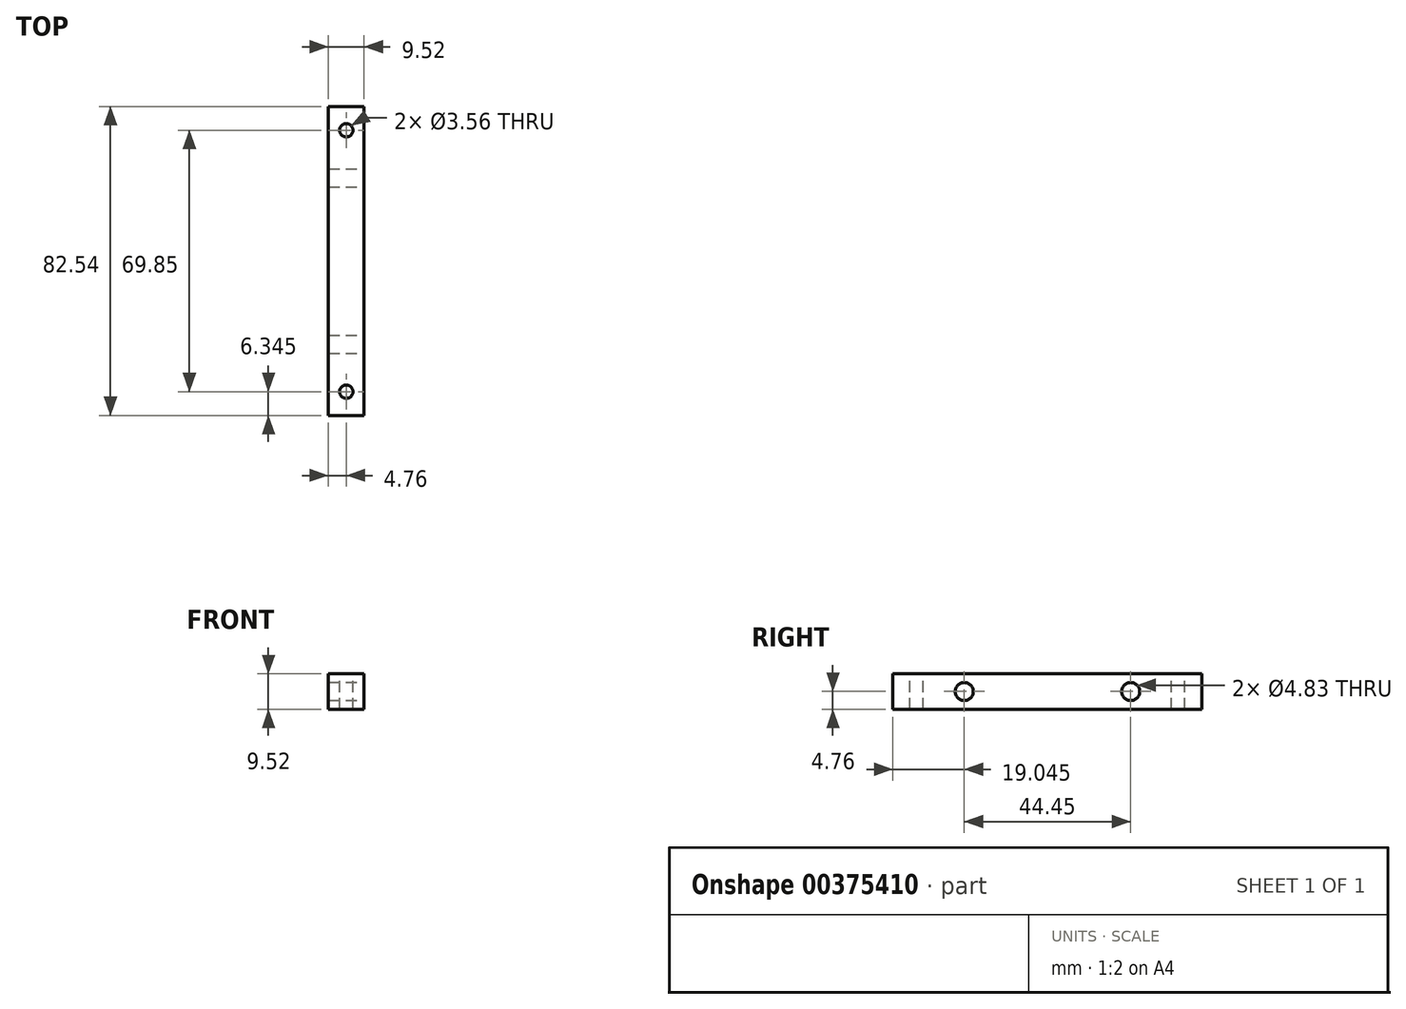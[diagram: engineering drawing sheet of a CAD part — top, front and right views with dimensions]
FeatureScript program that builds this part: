
annotation { "Feature Type Name" : "Feature", "Feature Type Description" : "" }
export const myFeature = defineFeature(function(context is Context, id is Id, definition is map)
    precondition{}
    {
        {
            var Q0;
            Q0=qCreatedBy(makeId("Front.planeOp"),FACE);
            var sketch = newSketch(context, id + "F0", { "sketchPlane" : qUnion([Q0])});
            skLineSegment(sketch, "E0.bottom", {"start": v(-4.76, 4.76) * mm, "end": v(4.76, 4.76) * mm});
            skLineSegment(sketch, "E0.top", {"start": v(-4.76, -4.76) * mm, "end": v(4.76, -4.76) * mm});
            skLineSegment(sketch, "E0.left", {"start": v(-4.76, 4.76) * mm, "end": v(-4.76, -4.76) * mm});
            skLineSegment(sketch, "E0.right", {"start": v(4.76, 4.76) * mm, "end": v(4.76, -4.76) * mm});
            skPoint(sketch, "E0.middle", {"position": v(0, 0) * mm});
            skSolve(sketch);
        }
        {
            var Q0;
            Q0=qSketchRegion(id+"F0",true);
            extrude(context, id + "F1", {"entities" : qUnion([Q0]), "depth" : 82.55 * mm, "symmetric" : true});
        }
        {
            var Q0;
            Q0=makeQuery(id+"F1.opExtrude","SWEPT_FACE",FACE,{"disambiguationData":[OSD([sQuery(id+"F0.wireOp",EDGE,"E0.bottom")])]});
            var sketch = newSketch(context, id + "F2", { "sketchPlane" : qUnion([Q0])});
            skLineSegment(sketch, "E1", {"start": v(0, 0) * mm, "end": v(0, -34.93) * mm, "construction": true});
            skCircle(sketch, "E2", {"center": v(0, -34.93) * mm, "radius": 1.78 * mm});
            skSolve(sketch);
        }
        {
            var Q0;
            Q0=qSketchRegion(id+"F2",true);
            extrude(context, id + "F3", {"entities" : qUnion([Q0]), "operationType" : NewBodyOperationType.REMOVE, "endBound" : BoundingType.THROUGH_ALL, "oppositeDirection" : true, "depth" : 25.4 * mm});
        }
        {
            var Q0;
            Q0=makeQuery(id+"F1.opExtrude","SWEPT_FACE",FACE,{"disambiguationData":[OSD([sQuery(id+"F0.wireOp",EDGE,"E0.bottom")])]});
            var sketch = newSketch(context, id + "F4", { "sketchPlane" : qUnion([Q0])});
            skLineSegment(sketch, "E3", {"start": v(0, 0) * mm, "end": v(0, 34.93) * mm, "construction": true});
            skCircle(sketch, "E4", {"center": v(0, 34.93) * mm, "radius": 1.78 * mm});
            skSolve(sketch);
        }
        {
            var Q0;
            Q0=qSketchRegion(id+"F4",true);
            extrude(context, id + "F5", {"entities" : qUnion([Q0]), "operationType" : NewBodyOperationType.REMOVE, "endBound" : BoundingType.THROUGH_ALL, "oppositeDirection" : true, "depth" : 25.4 * mm});
        }
        {
            var Q0;
            Q0=makeQuery(id+"F1.opExtrude","SWEPT_FACE",FACE,{"disambiguationData":[OSD([sQuery(id+"F0.wireOp",EDGE,"E0.right")])]});
            var sketch = newSketch(context, id + "F6", { "sketchPlane" : qUnion([Q0])});
            skLineSegment(sketch, "E5", {"start": v(0, 0) * mm, "end": v(-22.23, 0) * mm, "construction": true});
            skCircle(sketch, "E6", {"center": v(-22.23, 0) * mm, "radius": 2.41 * mm});
            skSolve(sketch);
        }
        {
            var Q0;
            Q0=qSketchRegion(id+"F6",true);
            extrude(context, id + "F7", {"entities" : qUnion([Q0]), "operationType" : NewBodyOperationType.REMOVE, "endBound" : BoundingType.THROUGH_ALL, "oppositeDirection" : true, "depth" : 25.4 * mm});
        }
        {
            var Q0;
            Q0=makeQuery(id+"F1.opExtrude","SWEPT_FACE",FACE,{"disambiguationData":[OSD([sQuery(id+"F0.wireOp",EDGE,"E0.right")])]});
            var sketch = newSketch(context, id + "F8", { "sketchPlane" : qUnion([Q0])});
            skLineSegment(sketch, "E7", {"start": v(0, 0) * mm, "end": v(22.22, 0) * mm, "construction": true});
            skCircle(sketch, "E8", {"center": v(22.22, 0) * mm, "radius": 2.41 * mm});
            skSolve(sketch);
        }
        {
            var Q0;
            Q0=qSketchRegion(id+"F8",true);
            extrude(context, id + "F9", {"entities" : qUnion([Q0]), "operationType" : NewBodyOperationType.REMOVE, "endBound" : BoundingType.THROUGH_ALL, "oppositeDirection" : true, "depth" : 25.4 * mm});
        }
    });
